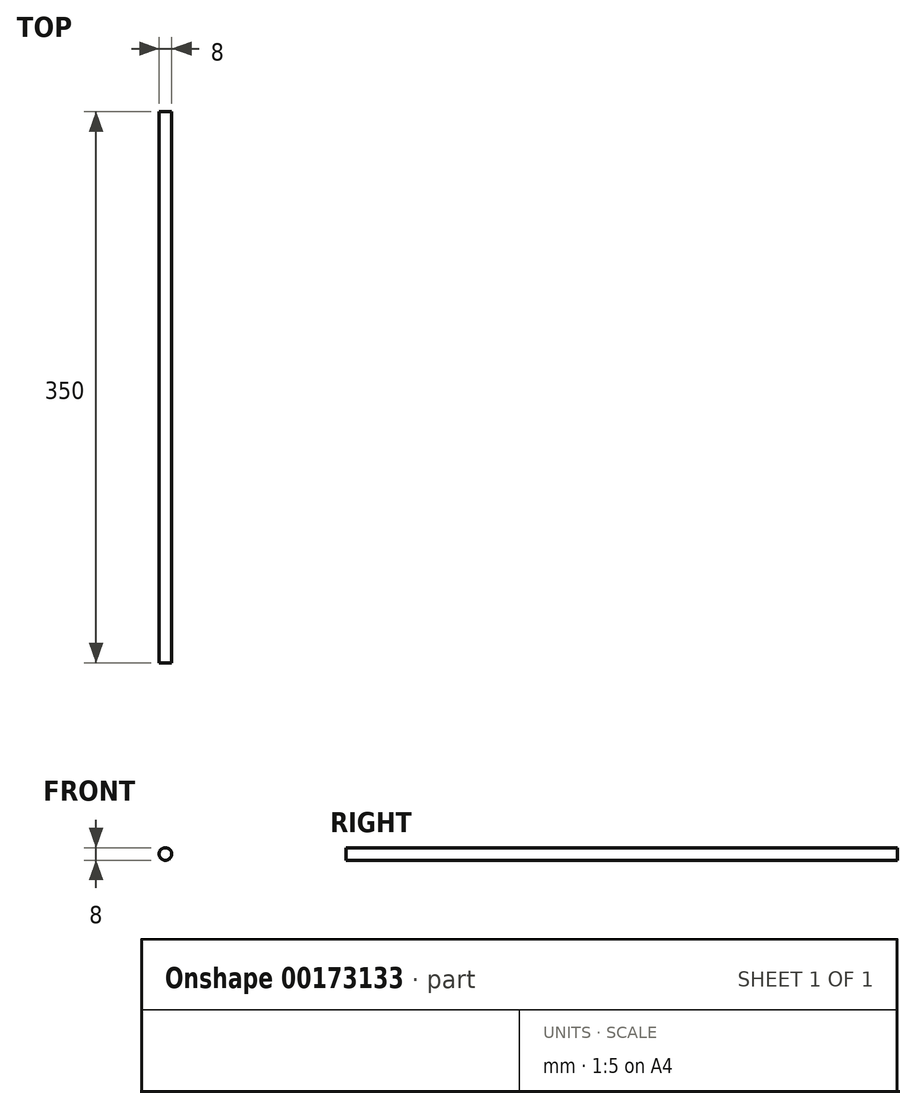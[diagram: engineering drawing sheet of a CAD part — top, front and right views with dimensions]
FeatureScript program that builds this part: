
annotation { "Feature Type Name" : "Feature", "Feature Type Description" : "" }
export const myFeature = defineFeature(function(context is Context, id is Id, definition is map)
    precondition{}
    {
        {
            var Q0;
            Q0=qCreatedBy(makeId("Front.planeOp"),FACE);
            var sketch = newSketch(context, id + "F0", { "sketchPlane" : qUnion([Q0])});
            skCircle(sketch, "E0", {"center": v(0, 0) * mm, "radius": 4 * mm});
            skCircle(sketch, "E1", {"center": v(0, 45) * mm, "radius": 4 * mm});
            skSolve(sketch);
        }
        {
            var Q0;
            Q0=makeQuery(id+"F0.imprint","IMPRINT",FACE,{"disambiguationData":[TD([[makeQuery(id+"F0.imprint","IMPRINT",EDGE,{"derivedFrom":sQuery(id+"F0.wireOp",EDGE,"E0")}),1.0]])]});
            extrude(context, id + "F1", {"entities" : qUnion([Q0]), "endBound" : BoundingType.SYMMETRIC, "depth" : 350 * mm});
        }
    });
